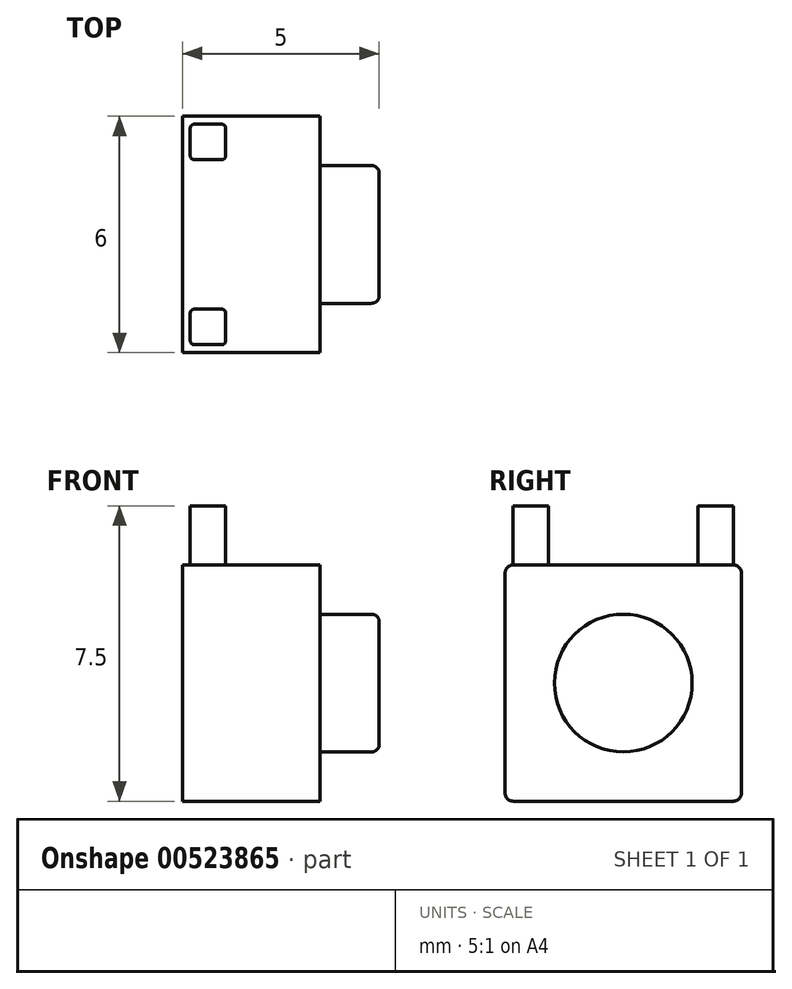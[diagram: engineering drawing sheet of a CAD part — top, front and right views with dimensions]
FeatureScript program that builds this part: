
annotation { "Feature Type Name" : "Feature", "Feature Type Description" : "" }
export const myFeature = defineFeature(function(context is Context, id is Id, definition is map)
    precondition{}
    {
        {
            var Q0;
            Q0=qCreatedBy(makeId("Right.planeOp"),FACE);
            var sketch = newSketch(context, id + "F0", { "sketchPlane" : qUnion([Q0])});
            skLineSegment(sketch, "E0.bottom", {"start": v(-3, 3) * mm, "end": v(3, 3) * mm});
            skLineSegment(sketch, "E0.top", {"start": v(-3, -3) * mm, "end": v(3, -3) * mm});
            skLineSegment(sketch, "E0.left", {"start": v(-3, 3) * mm, "end": v(-3, -3) * mm});
            skLineSegment(sketch, "E0.right", {"start": v(3, 3) * mm, "end": v(3, -3) * mm});
            skPoint(sketch, "E0.middle", {"position": v(0, 0) * mm});
            skSolve(sketch);
        }
        {
            var Q0;
            Q0 = qSketchRegion(id + "F0", true);
            extrude(context, id + "F1", {"entities" : qUnion([Q0]), "endBound" : BoundingType.SYMMETRIC, "depth" : 3.5 * mm, "offsetDistance" : 25 * mm});
        }
        {
            var Q0;
            Q0=makeQuery(id+"F1.opExtrude","CAP_FACE",FACE,{"disambiguationData":[OSD([sQuery(id+"F0.wireOp",EDGE,"E0.bottom"),sQuery(id+"F0.wireOp",EDGE,"E0.top"),sQuery(id+"F0.wireOp",EDGE,"E0.left"),sQuery(id+"F0.wireOp",EDGE,"E0.right")])],"isStart":false});
            var sketch = newSketch(context, id + "F2", { "sketchPlane" : qUnion([Q0])});
            skCircle(sketch, "E1", {"center": v(0, 0) * mm, "radius": 1.75 * mm});
            skSolve(sketch);
        }
        {
            var Q0;
            Q0=makeQuery(id+"F2.imprint","IMPRINT",FACE,{"disambiguationData":[TD([[makeQuery(id+"F2.imprint","IMPRINT",EDGE,{"derivedFrom":sQuery(id+"F2.wireOp",EDGE,"E1")}),1.0]])]});
            extrude(context, id + "F3", {"entities" : qUnion([Q0]), "operationType" : NewBodyOperationType.ADD, "depth" : 1.5 * mm, "offsetDistance" : 25 * mm});
        }
        {
            var Q0;
            Q0=makeQuery(id+"F3.opExtrude","CAP_EDGE",EDGE,{"disambiguationData":[OSD([sQuery(id+"F2.wireOp",EDGE,"E1")])],"isStart":false});
            var Q1;
            Q1=makeQuery(id+"F1.opExtrude","SWEPT_EDGE",EDGE,{"disambiguationData":[OSD([sQuery(id+"F0.wireOp",EDGE,"E0.bottom"),sQuery(id+"F0.wireOp",EDGE,"E0.left")])]});
            var Q2;
            Q2=makeQuery(id+"F1.opExtrude","SWEPT_EDGE",EDGE,{"disambiguationData":[OSD([sQuery(id+"F0.wireOp",EDGE,"E0.bottom"),sQuery(id+"F0.wireOp",EDGE,"E0.right")])]});
            var Q3;
            Q3=makeQuery(id+"F1.opExtrude","SWEPT_EDGE",EDGE,{"disambiguationData":[OSD([sQuery(id+"F0.wireOp",EDGE,"E0.top"),sQuery(id+"F0.wireOp",EDGE,"E0.right")])]});
            var Q4;
            Q4=makeQuery(id+"F1.opExtrude","SWEPT_EDGE",EDGE,{"disambiguationData":[OSD([sQuery(id+"F0.wireOp",EDGE,"E0.top"),sQuery(id+"F0.wireOp",EDGE,"E0.left")])]});
            fillet(context, id + "F4", {"entities" : qUnion([Q0, Q1, Q2, Q3, Q4]), "radius" : .2 * mm, "tangentPropagation" : true, "allowEdgeOverflow" : false});
        }
        {
            var Q0;
            Q0=makeQuery(id+"F1.opExtrude","SWEPT_FACE",FACE,{"disambiguationData":[OSD([sQuery(id+"F0.wireOp",EDGE,"E0.bottom")])]});
            var sketch = newSketch(context, id + "F5", { "sketchPlane" : qUnion([Q0])});
            skLineSegment(sketch, "E2.bottom", {"start": v(-1.45, -2.8) * mm, "end": v(-0.75, -2.8) * mm});
            skLineSegment(sketch, "E2.top", {"start": v(-1.45, -1.9) * mm, "end": v(-0.75, -1.9) * mm});
            skLineSegment(sketch, "E2.left", {"start": v(-1.55, -2.7) * mm, "end": v(-1.55, -2) * mm});
            skLineSegment(sketch, "E2.right", {"start": v(-0.65, -2.7) * mm, "end": v(-0.65, -2) * mm});
            skPoint(sketch, "E3.visualSharp", {"position": v(-1.55, -1.9) * mm});
            skArc(sketch, "E3.filletArc", {"start": v(-1.45, -1.9) * mm, "mid": v(-1.52, -1.93) * mm, "end": v(-1.55, -2) * mm});
            skPoint(sketch, "E4.visualSharp", {"position": v(-0.65, -1.9) * mm});
            skArc(sketch, "E4.filletArc", {"start": v(-0.65, -2) * mm, "mid": v(-0.68, -1.93) * mm, "end": v(-0.75, -1.9) * mm});
            skPoint(sketch, "E5.visualSharp", {"position": v(-0.65, -2.8) * mm});
            skArc(sketch, "E5.filletArc", {"start": v(-0.75, -2.8) * mm, "mid": v(-0.68, -2.77) * mm, "end": v(-0.65, -2.7) * mm});
            skPoint(sketch, "E6.visualSharp", {"position": v(-1.55, -2.8) * mm});
            skArc(sketch, "E6.filletArc", {"start": v(-1.55, -2.7) * mm, "mid": v(-1.52, -2.77) * mm, "end": v(-1.45, -2.8) * mm});
            skArc(sketch, "E7.MirrorCS", {"start": v(-0.75, 2.8) * mm, "mid": v(-0.68, 2.77) * mm, "end": v(-0.65, 2.7) * mm});
            skLineSegment(sketch, "E8.MirrorCS", {"start": v(-1.45, 1.9) * mm, "end": v(-0.75, 1.9) * mm});
            skLineSegment(sketch, "E9.MirrorCS", {"start": v(-1.55, 2.7) * mm, "end": v(-1.55, 2) * mm});
            skArc(sketch, "E10.MirrorCS", {"start": v(-1.55, 2.7) * mm, "mid": v(-1.52, 2.77) * mm, "end": v(-1.45, 2.8) * mm});
            skLineSegment(sketch, "E11.MirrorCS", {"start": v(-0.65, 2.7) * mm, "end": v(-0.65, 2) * mm});
            skLineSegment(sketch, "E12.MirrorCS", {"start": v(-1.45, 2.8) * mm, "end": v(-0.75, 2.8) * mm});
            skArc(sketch, "E13.MirrorCS", {"start": v(-1.45, 1.9) * mm, "mid": v(-1.52, 1.93) * mm, "end": v(-1.55, 2) * mm});
            skArc(sketch, "E14.MirrorCS", {"start": v(-0.65, 2) * mm, "mid": v(-0.68, 1.93) * mm, "end": v(-0.75, 1.9) * mm});
            skPoint(sketch, "E15.MirrorP", {"position": v(-1.55, 1.9) * mm});
            skPoint(sketch, "E16.MirrorP", {"position": v(-0.65, 1.9) * mm});
            skPoint(sketch, "E17.MirrorP", {"position": v(-0.65, 2.8) * mm});
            skPoint(sketch, "E18.MirrorP", {"position": v(-1.55, 2.8) * mm});
            skSolve(sketch);
        }
        {
            var Q0;
            Q0 = qSketchRegion(id + "F5", true);
            extrude(context, id + "F6", {"entities" : qUnion([Q0]), "operationType" : NewBodyOperationType.ADD, "depth" : 1.5 * mm, "offsetDistance" : 25 * mm});
        }
    });
